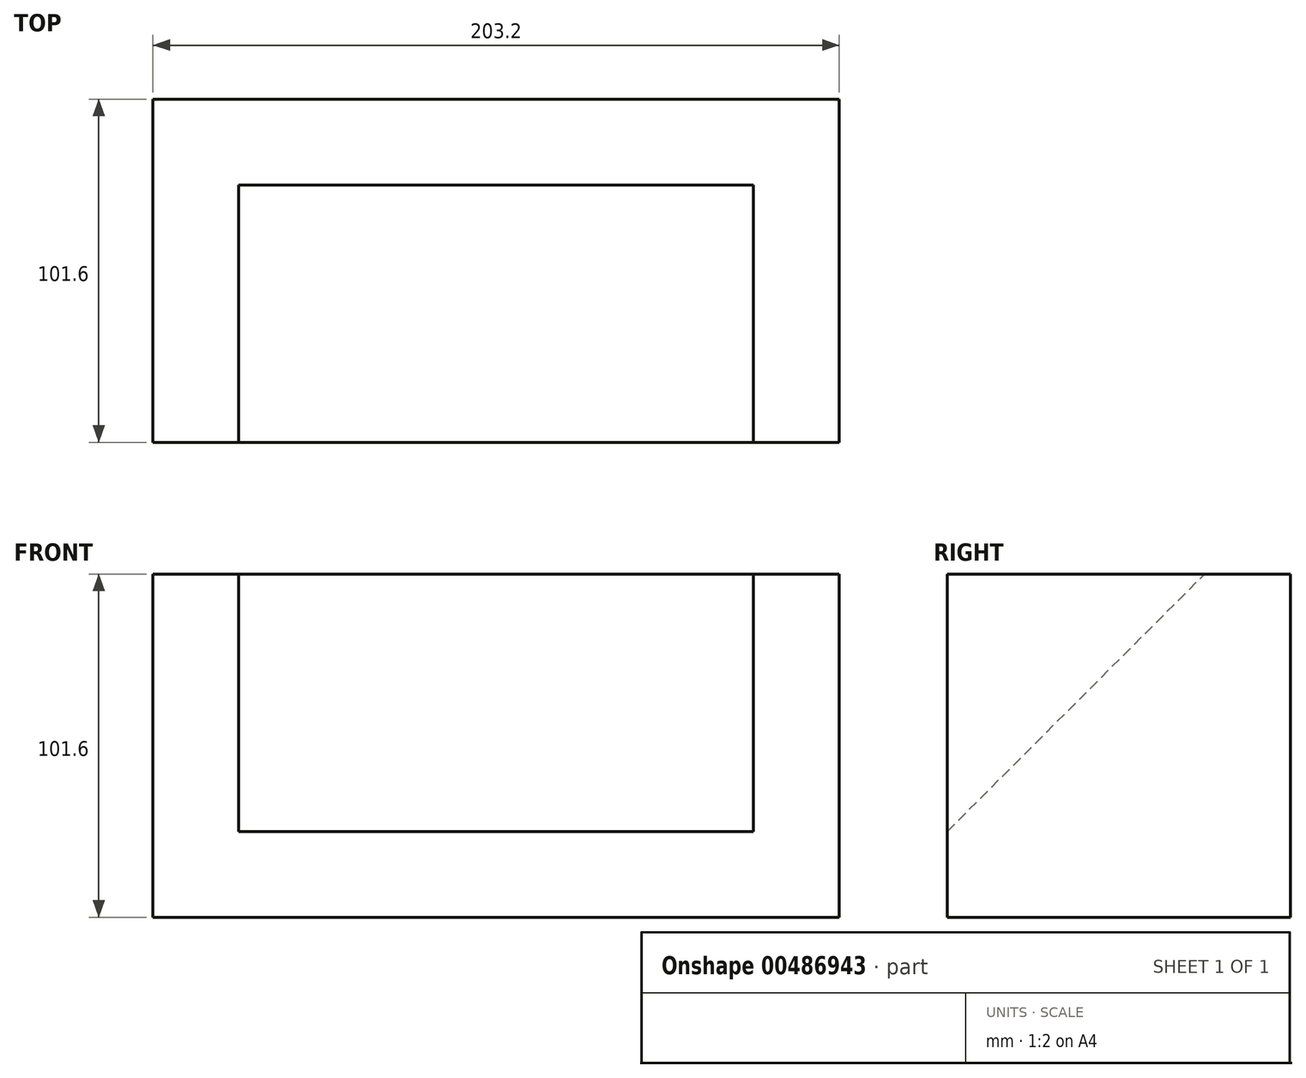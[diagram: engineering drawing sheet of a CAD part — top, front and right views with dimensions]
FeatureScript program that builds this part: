
annotation { "Feature Type Name" : "Feature", "Feature Type Description" : "" }
export const myFeature = defineFeature(function(context is Context, id is Id, definition is map)
    precondition{}
    {
        {
            var Q0;
            Q0=qCreatedBy(makeId("Front.planeOp"),FACE);
            var sketch = newSketch(context, id + "F0", { "sketchPlane" : qUnion([Q0])});
            skLineSegment(sketch, "E0.bottom", {"start": v(-101.6, 50.8) * mm, "end": v(101.6, 50.8) * mm});
            skLineSegment(sketch, "E0.top", {"start": v(-101.6, -50.8) * mm, "end": v(101.6, -50.8) * mm});
            skLineSegment(sketch, "E0.left", {"start": v(-101.6, 50.8) * mm, "end": v(-101.6, -50.8) * mm});
            skLineSegment(sketch, "E0.right", {"start": v(101.6, 50.8) * mm, "end": v(101.6, -50.8) * mm});
            skPoint(sketch, "E0.middle", {"position": v(0, 0) * mm});
            skSolve(sketch);
        }
        {
            var Q0;
            Q0 = qSketchRegion(id + "F0", true);
            extrude(context, id + "F1", {"entities" : qUnion([Q0]), "depth" : 101.6 * mm});
        }
        {
            var Q0;
            Q0=makeQuery(id+"F1.opExtrude","CAP_FACE",FACE,{"disambiguationData":[OSD([sQuery(id+"F0.wireOp",EDGE,"E0.bottom"),sQuery(id+"F0.wireOp",EDGE,"E0.top"),sQuery(id+"F0.wireOp",EDGE,"E0.left"),sQuery(id+"F0.wireOp",EDGE,"E0.right")])],"isStart":false});
            var sketch = newSketch(context, id + "F2", { "sketchPlane" : qUnion([Q0])});
            skLineSegment(sketch, "E1.bottom", {"start": v(-76.2, 50.8) * mm, "end": v(76.2, 50.8) * mm});
            skLineSegment(sketch, "E1.top", {"start": v(-76.2, -25.4) * mm, "end": v(76.2, -25.4) * mm});
            skLineSegment(sketch, "E1.left", {"start": v(-76.2, 50.8) * mm, "end": v(-76.2, -25.4) * mm});
            skLineSegment(sketch, "E1.right", {"start": v(76.2, 50.8) * mm, "end": v(76.2, -25.4) * mm});
            skPoint(sketch, "E1.middle", {"position": v(0, 12.7) * mm});
            skSolve(sketch);
        }
        {
            var Q0;
            Q0 = qSketchRegion(id + "F2", true);
            extrude(context, id + "F3", {"entities" : qUnion([Q0]), "operationType" : NewBodyOperationType.REMOVE, "oppositeDirection" : true, "depth" : 76.2 * mm});
        }
        {
            var Q0;
            Q0=makeQuery(id+"F3.boolean.opBoolean","COPY",FACE,{"derivedFrom":makeQuery(id+"F3.opExtrude","SWEPT_FACE",FACE,{"disambiguationData":[OSD([sQuery(id+"F2.wireOp",EDGE,"E1.right")])]})});
            var sketch = newSketch(context, id + "F4", { "sketchPlane" : qUnion([Q0])});
            skLineSegment(sketch, "E2", {"start": v(101.6, -25.4) * mm, "end": v(25.4, 50.8) * mm});
            skLineSegment(sketch, "E3", {"start": v(25.4, 50.8) * mm, "end": v(25.4, -25.4) * mm});
            skLineSegment(sketch, "E4", {"start": v(25.4, -25.4) * mm, "end": v(101.6, -25.4) * mm});
            skSolve(sketch);
        }
        {
            var Q0;
            Q0 = qSketchRegion(id + "F4", true);
            extrude(context, id + "F5", {"entities" : qUnion([Q0]), "operationType" : NewBodyOperationType.ADD, "depth" : 152.4 * mm});
        }
    });
